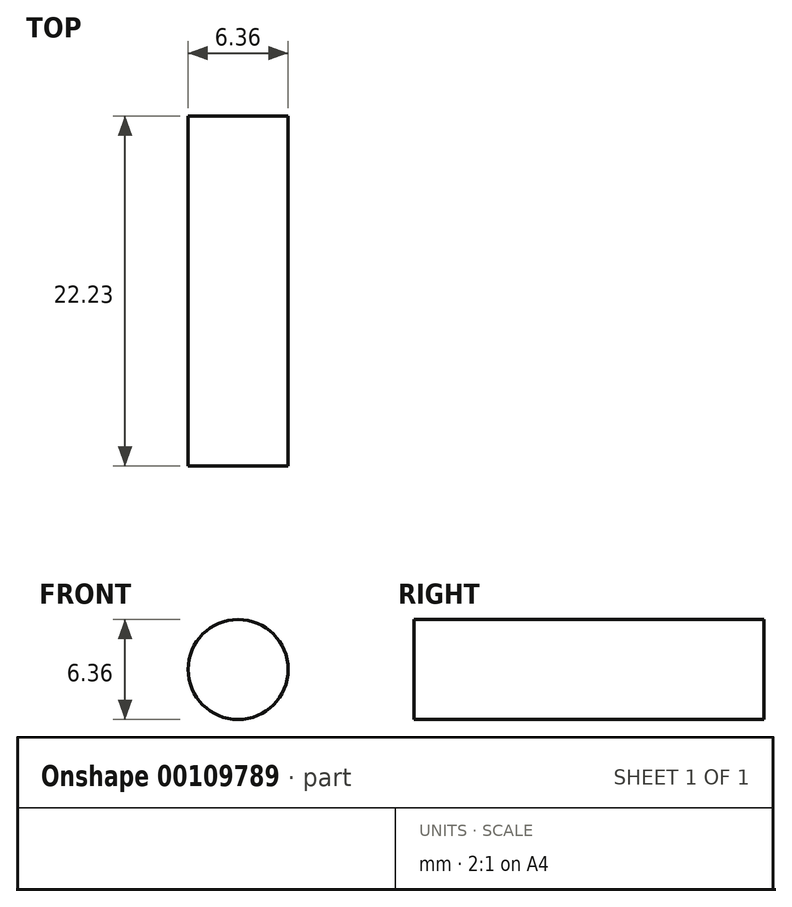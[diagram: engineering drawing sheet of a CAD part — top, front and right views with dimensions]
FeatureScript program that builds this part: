
annotation { "Feature Type Name" : "Feature", "Feature Type Description" : "" }
export const myFeature = defineFeature(function(context is Context, id is Id, definition is map)
    precondition{}
    {
        {
            var Q0;
            Q0=qCreatedBy(makeId("Front.planeOp"),FACE);
            var sketch = newSketch(context, id + "F0", { "sketchPlane" : qUnion([Q0])});
            skCircle(sketch, "E0", {"center": v(0, 0) * mm, "radius": 3.18 * mm});
            skSolve(sketch);
        }
        {
            var Q0;
            Q0 = qSketchRegion(id + "F0", true);
            extrude(context, id + "F1", {"entities" : qUnion([Q0]), "depth" : 22.22 * mm});
        }
    });
